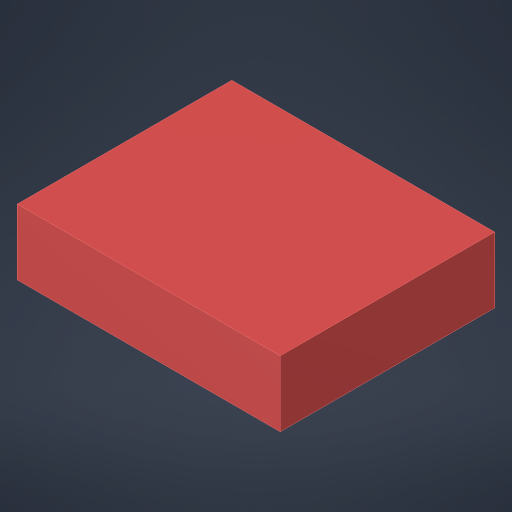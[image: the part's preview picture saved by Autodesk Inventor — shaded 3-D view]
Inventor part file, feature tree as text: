
AUTODESK INVENTOR PART (.ipt)
format: ipt  version: 2023.4 (Build 274418000, 418)  size: 140,288 bytes
history: native  units: in
note: dims shown in document units (in); Inventor stores cm internally (conversion verified against a paired STEP export)
features: extrude x1, sketch x1
ambient origin geometry x8: Origin, YZ Plane, XZ Plane, XY Plane, X Axis, Y Axis, Z Axis, Center Point
bodies: Solid1 (feature_tree)
feature tree (2):
  extrude  "Extrusion1"  Depth=15.5in
  sketch  "Sketch1"  dims[d0=19.0in d1=15.5in d2=4.75in d3=0.0in]
